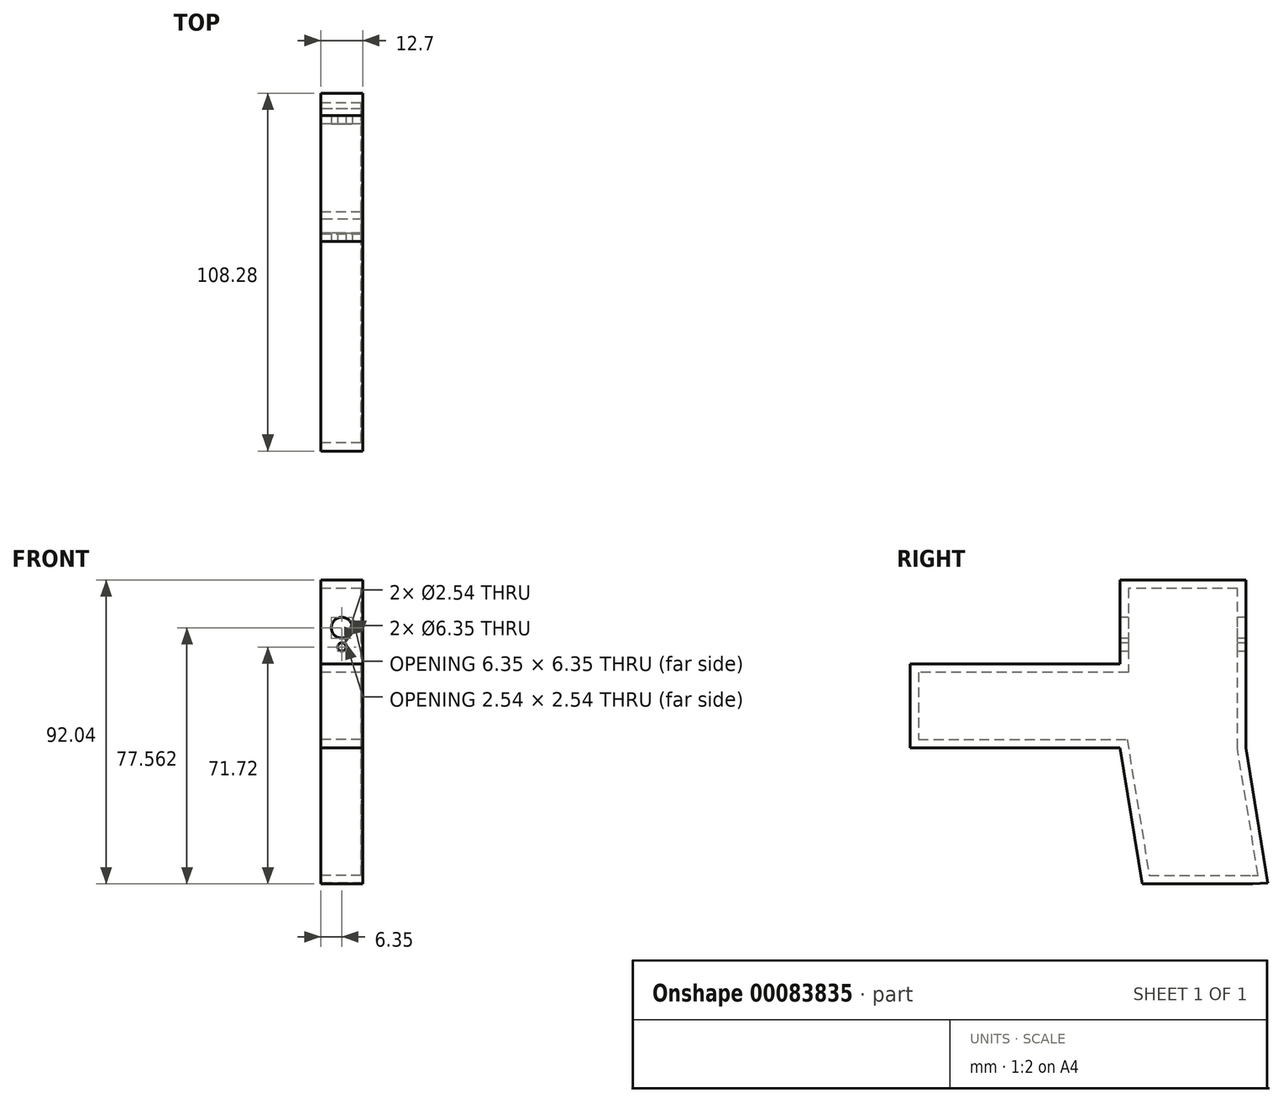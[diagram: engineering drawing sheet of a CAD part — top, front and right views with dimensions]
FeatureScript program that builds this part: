
annotation { "Feature Type Name" : "Feature", "Feature Type Description" : "" }
export const myFeature = defineFeature(function(context is Context, id is Id, definition is map)
    precondition{}
    {
        {
            var Q0;
            Q0=qCreatedBy(makeId("Right.planeOp"),FACE);
            var sketch = newSketch(context, id + "F0", { "sketchPlane" : qUnion([Q0])});
            skLineSegment(sketch, "E0.bottom", {"start": v(-49.52, 10.6) * mm, "end": v(13.98, 10.6) * mm});
            skLineSegment(sketch, "E0.top", {"start": v(-49.52, -14.8) * mm, "end": v(13.98, -14.8) * mm});
            skLineSegment(sketch, "E0.left", {"start": v(-49.52, 10.6) * mm, "end": v(-49.52, -14.8) * mm});
            skLineSegment(sketch, "E0.right", {"start": v(52.08, 10.6) * mm, "end": v(52.08, -14.8) * mm});
            skLineSegment(sketch, "E1.top", {"start": v(54.08, -56.05) * mm, "end": v(20.7, -56.05) * mm});
            skLineSegment(sketch, "E2", {"start": v(20.7, -56.05) * mm, "end": v(13.98, -14.8) * mm});
            skLineSegment(sketch, "E3", {"start": v(52.08, -14.8) * mm, "end": v(58.76, -55.76) * mm});
            skLineSegment(sketch, "E4", {"start": v(58.76, -55.76) * mm, "end": v(54.08, -56.05) * mm});
            skLineSegment(sketch, "E5.top", {"start": v(13.98, 36) * mm, "end": v(52.08, 36) * mm});
            skLineSegment(sketch, "E5.left", {"start": v(13.98, 10.6) * mm, "end": v(13.98, 36) * mm});
            skLineSegment(sketch, "E5.right", {"start": v(52.08, 10.6) * mm, "end": v(52.08, 36) * mm});
            skSolve(sketch);
        }
        {
            var Q0;
            Q0=qCreatedBy(makeId("Right.planeOp"),FACE);
            var sketch = newSketch(context, id + "F1", { "sketchPlane" : qUnion([Q0])});
            skLineSegment(sketch, "E6.0", {"start": v(22.87, -53.5) * mm, "end": v(54, -53.5) * mm});
            skLineSegment(sketch, "E6.1", {"start": v(16.14, -12.27) * mm, "end": v(22.87, -53.5) * mm});
            skLineSegment(sketch, "E6.2", {"start": v(-46.98, -12.27) * mm, "end": v(16.14, -12.27) * mm});
            skLineSegment(sketch, "E6.3", {"start": v(-46.98, 8.05) * mm, "end": v(-46.98, -12.27) * mm});
            skLineSegment(sketch, "E6.4", {"start": v(16.52, 8.05) * mm, "end": v(-46.98, 8.05) * mm});
            skLineSegment(sketch, "E6.5", {"start": v(54, -53.5) * mm, "end": v(55.8, -53.4) * mm});
            skLineSegment(sketch, "E6.6", {"start": v(55.8, -53.4) * mm, "end": v(49.54, -15.02) * mm});
            skLineSegment(sketch, "E6.7", {"start": v(49.54, -15.02) * mm, "end": v(49.54, 10.6) * mm});
            skLineSegment(sketch, "E6.8", {"start": v(49.54, 10.6) * mm, "end": v(49.54, 33.45) * mm});
            skLineSegment(sketch, "E6.9", {"start": v(49.54, 33.45) * mm, "end": v(16.52, 33.45) * mm});
            skLineSegment(sketch, "E6.10", {"start": v(16.52, 33.45) * mm, "end": v(16.52, 8.05) * mm});
            skSolve(sketch);
        }
        {
            var Q0;
            Q0=makeQuery(id+"F0.imprint","IMPRINT",FACE,{"disambiguationData":[TD([[makeQuery(id+"F0.imprint","IMPRINT",EDGE,{"derivedFrom":sQuery(id+"F0.wireOp",EDGE,"E0.bottom")}),-1.0]])]});
            extrude(context, id + "F2", {"entities" : qUnion([Q0]), "depth" : 12.7 * mm});
        }
        {
            var Q0;
            Q0=makeQuery(id+"F1.imprint","IMPRINT",FACE,{"disambiguationData":[TD([[makeQuery(id+"F1.imprint","IMPRINT",EDGE,{"derivedFrom":sQuery(id+"F1.wireOp",EDGE,"E6.0")}),1.0]])]});
            extrude(context, id + "F3", {"entities" : qUnion([Q0]), "operationType" : NewBodyOperationType.REMOVE, "depth" : 12.2 * mm});
        }
        {
            var Q0;
            Q0=makeQuery(id+"F2.opExtrude","SWEPT_FACE",FACE,{"disambiguationData":[OSD([sQuery(id+"F0.wireOp",EDGE,"E5.left")])]});
            var sketch = newSketch(context, id + "F4", { "sketchPlane" : qUnion([Q0])});
            skCircle(sketch, "E7", {"center": v(6.35, 15.67) * mm, "radius": 1.27 * mm});
            skSolve(sketch);
        }
        {
            var Q0;
            Q0=makeQuery(id+"F4.imprint","IMPRINT",FACE,{"disambiguationData":[TD([[makeQuery(id+"F4.imprint","IMPRINT",EDGE,{"derivedFrom":sQuery(id+"F4.wireOp",EDGE,"E7")}),1.0]])]});
            var Q1;
            Q1=sQuery(id+"F4.wireOp",EDGE,"E7");
            extrude(context, id + "F5", {"entities" : qUnion([Q0]), "operationType" : NewBodyOperationType.REMOVE, "surfaceEntities" : qUnion([Q1]), "oppositeDirection" : true, "depth" : 38.24 * mm});
        }
        {
            var Q0;
            Q0=makeQuery(id+"F2.opExtrude","SWEPT_FACE",FACE,{"disambiguationData":[OSD([sQuery(id+"F0.wireOp",EDGE,"E5.left")])]});
            var sketch = newSketch(context, id + "F6", { "sketchPlane" : qUnion([Q0])});
            skCircle(sketch, "E8", {"center": v(6.35, 21.51) * mm, "radius": 3.18 * mm});
            skCircle(sketch, "E9.0", {"center": v(6.35, 15.67) * mm, "radius": 1.27 * mm});
            skLineSegment(sketch, "E10", {"start": v(6.35, 10.6) * mm, "end": v(6.35, 36) * mm, "construction": true});
            skSolve(sketch);
        }
        {
            var Q0;
            Q0=makeQuery(id+"F6.imprint","IMPRINT",FACE,{"disambiguationData":[TD([[makeQuery(id+"F6.imprint","IMPRINT",EDGE,{"derivedFrom":sQuery(id+"F6.wireOp",EDGE,"E8")}),1.0]])]});
            extrude(context, id + "F7", {"entities" : qUnion([Q0]), "operationType" : NewBodyOperationType.REMOVE, "oppositeDirection" : true, "depth" : 38.23 * mm});
        }
    });
